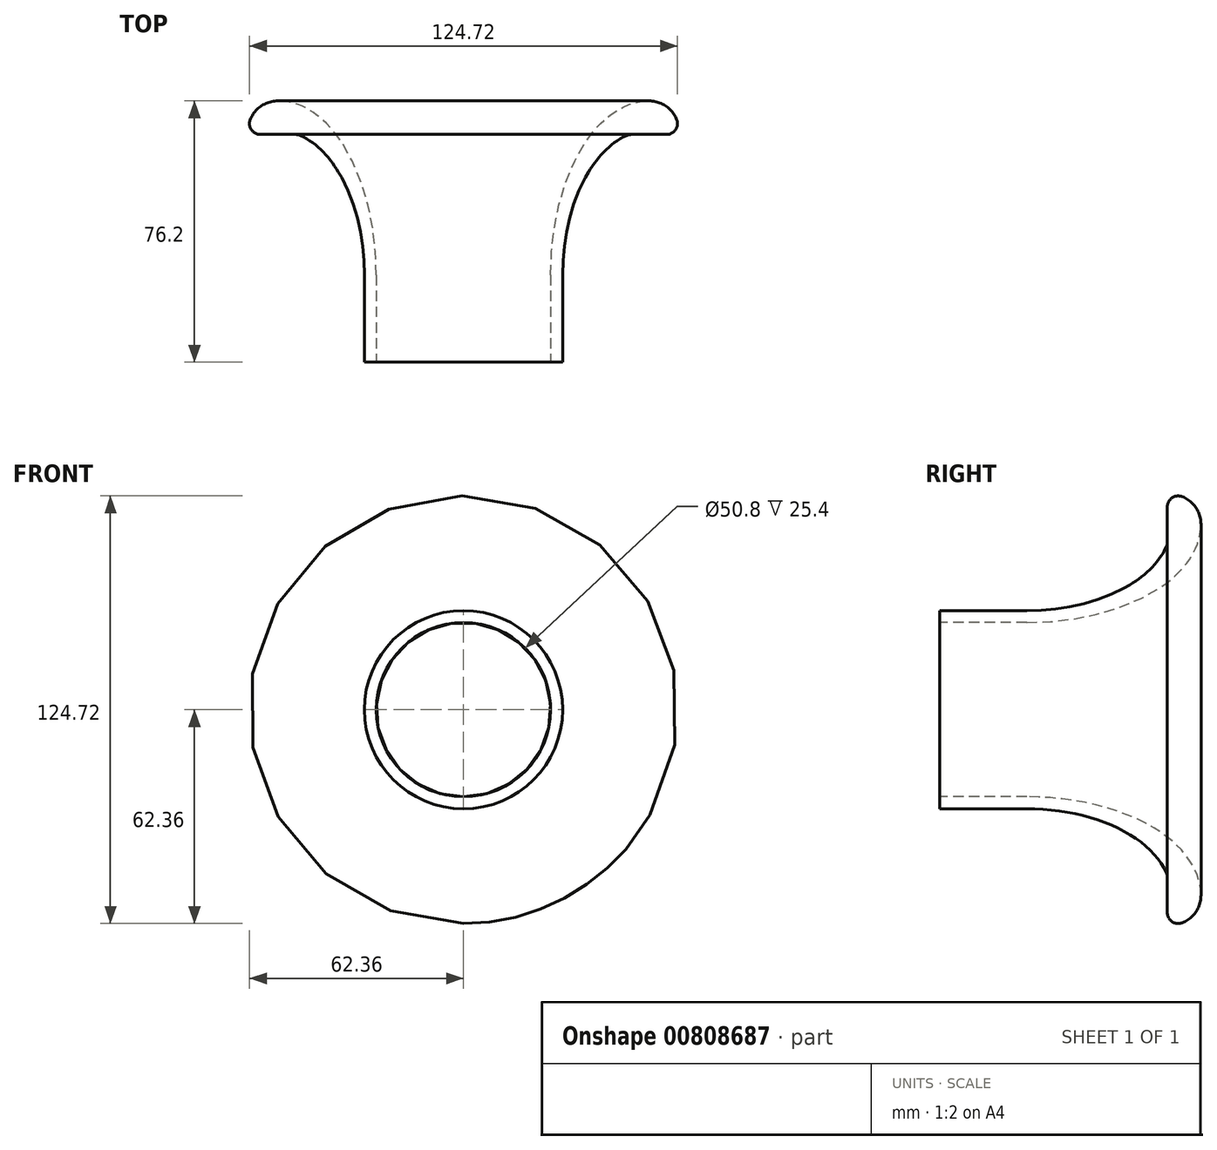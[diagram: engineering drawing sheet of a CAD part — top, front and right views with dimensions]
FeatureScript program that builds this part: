
annotation { "Feature Type Name" : "Feature", "Feature Type Description" : "" }
export const myFeature = defineFeature(function(context is Context, id is Id, definition is map)
    precondition{}
    {
        {
            var Q0;
            Q0=qCreatedBy(makeId("Top.planeOp"),FACE);
            var sketch = newSketch(context, id + "F0", { "sketchPlane" : qUnion([Q0])});
            skLineSegment(sketch, "E0", {"start": v(0, 0) * mm, "end": v(0, 70.34) * mm, "construction": true});
            skArc(sketch, "E1", {"start": v(62.14, 45.33) * mm, "mid": v(58.96, 49.3) * mm, "end": v(54.1, 50.8) * mm});
            skEllipticalArc(sketch, "E2", {});
            skLineSegment(sketch, "E3", {"start": v(28.9, 0) * mm, "end": v(28.9, -25.4) * mm});
            skLineSegment(sketch, "E4", {"start": v(28.9, -25.4) * mm, "end": v(25.4, -25.4) * mm});
            skLineSegment(sketch, "E5", {"start": v(25.4, -25.4) * mm, "end": v(25.4, 0) * mm});
            skEllipticalArc(sketch, "E6", {});
            skArc(sketch, "E7", {"start": v(59.18, 41) * mm, "mid": v(61.8, 42.38) * mm, "end": v(62.14, 45.33) * mm});
            skLineSegment(sketch, "E8", {"start": v(59.18, 41) * mm, "end": v(48.85, 41) * mm});
            skArc(sketch, "E9.filletArc", {"start": v(48.85, 41) * mm, "mid": v(48.18, 40.92) * mm, "end": v(47.55, 40.71) * mm});
            skLineSegment(sketch, "E10", {"start": v(0, 0) * mm, "end": v(25.4, 0) * mm, "construction": true});
            const initialGuessF0  = {"E2": [0.054102, 0, 0, 1, 0.0508, 0.028702, 0, 1.5707963267948966], "E6": [0.054102, 0, 0, 1, 0.042164, 0.025209500000000155, 0.26305170816144885, 1.5707963267948966]};
            skSetInitialGuess(sketch, initialGuessF0);
            skSolve(sketch);
        }
        {
            var Q0;
            Q0=qSketchRegion(id+"F0",true);
            var Q1;
            Q1=sQuery(id+"F0.wireOp",EDGE,"E0");
            revolve(context, id + "F1", {"surfaceOperationType" : NewSurfaceOperationType.NEW, "entities" : qUnion([Q0]), "axis" : qUnion([Q1]), "revolveType" : RevolveType.FULL});
        }
    });
